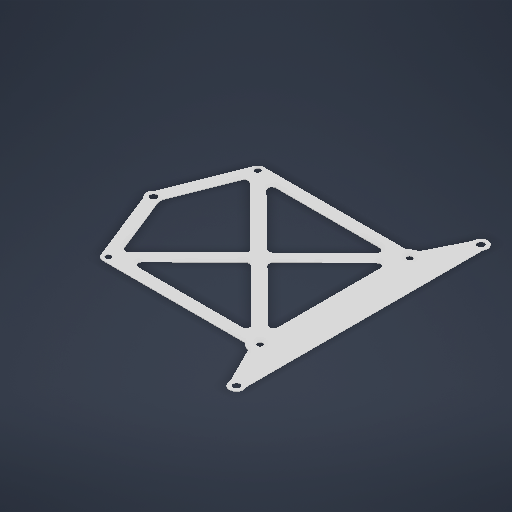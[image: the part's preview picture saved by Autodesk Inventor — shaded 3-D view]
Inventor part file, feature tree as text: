
AUTODESK INVENTOR PART (.ipt)
format: ipt  version: 2025 (Build 290162000, 162)  size: 343,040 bytes
history: native  units: mm
features: reference x5, other x4, sheet_metal_op x1, chamfer x1, sketch x1
ambient origin geometry x8: Origin, YZ Plane, XZ Plane, XY Plane, X Axis, Y Axis, Z Axis, Center Point
bodies: Solid1 (feature_tree)
feature tree (12):
  sheet_metal_op  "Face1"
  chamfer  "Corner Round2"
  sketch  "Sketch1"  dims[d11=6.0mm d12=6.0mm d14=10.826mm d15=10.826mm d16=10.826mm d17=12.0mm d18=10.826mm d19=12.0mm d20=12.0mm d38=0.5mm d39=20.0mm d40=10.0mm d41=10.0mm d44=12.0mm d45=12.0mm d46=12.0mm d47=10.0mm d48=10.0mm d49=10.0mm d50=10.0mm d51=10.0mm d52=10.0mm d53=10.0mm d54=10.0mm d55=10.0mm d56=10.0mm d58=18.0mm d59=18.0mm d60=3.175mm]
  reference  "Reference5"
  reference  "Reference6"
  reference  "Reference7"
  reference  "Reference8"
  reference  "Reference9"
  other  "Plate1"
  other  "<userpath> 7 was better\Documents\makerbot stuff\cad\bed.iam"
  other  "bed.iam"
  other  "bed_plate:1"
